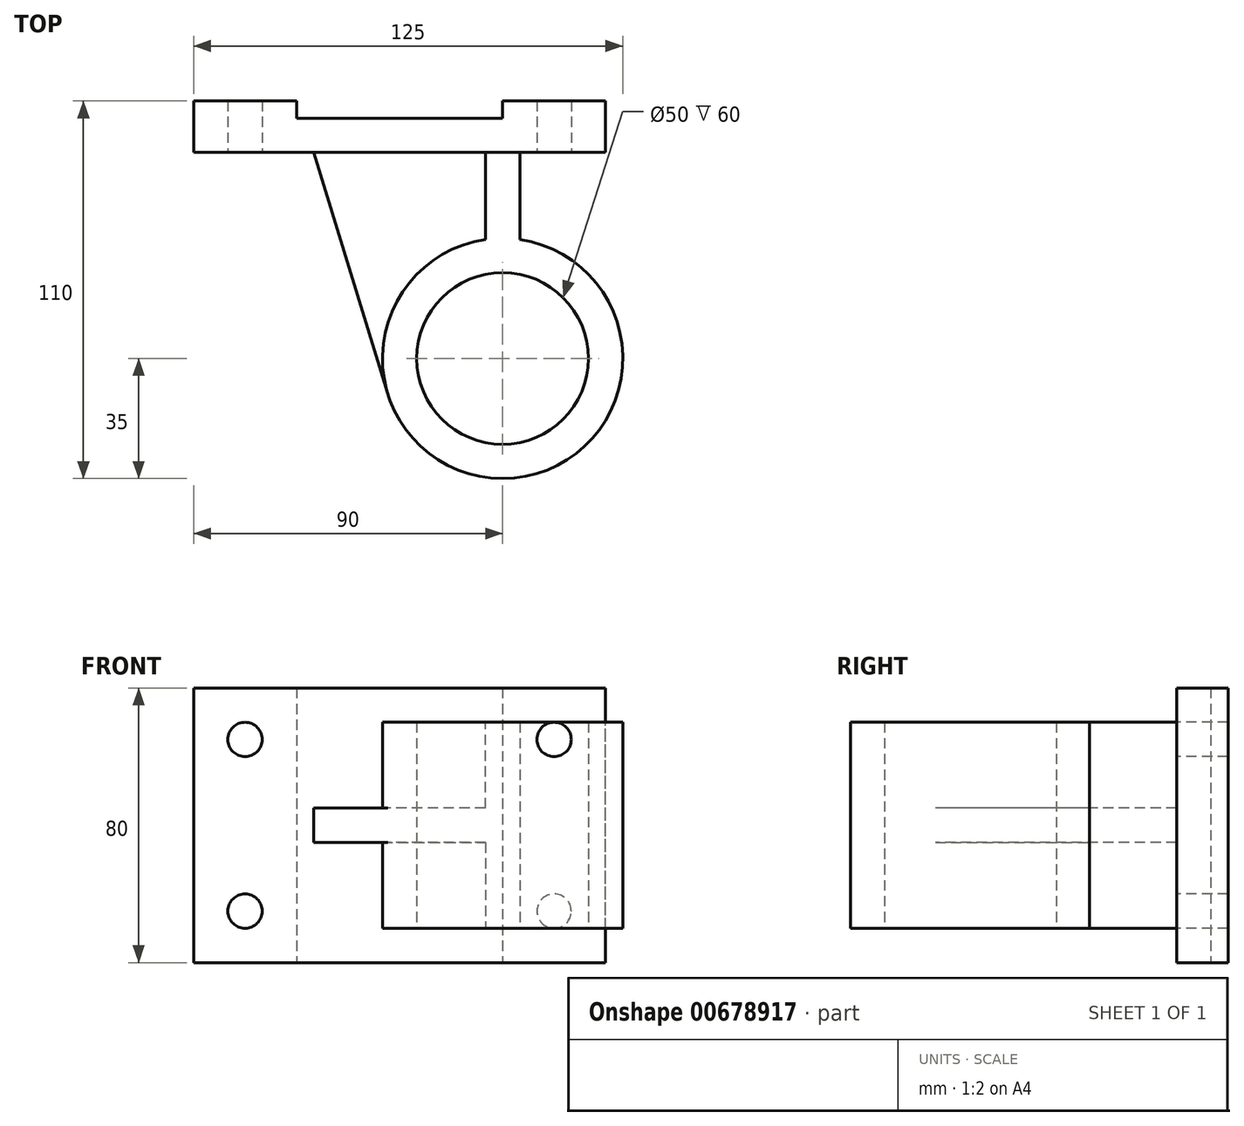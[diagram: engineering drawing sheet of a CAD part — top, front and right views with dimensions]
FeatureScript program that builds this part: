
annotation { "Feature Type Name" : "Feature", "Feature Type Description" : "" }
export const myFeature = defineFeature(function(context is Context, id is Id, definition is map)
    precondition{}
    {
        {
            var Q0;
            Q0=qCreatedBy(makeId("Front.planeOp"),FACE);
            var sketch = newSketch(context, id + "F0", { "sketchPlane" : qUnion([Q0])});
            skLineSegment(sketch, "E0.bottom", {"start": v(0, 0) * mm, "end": v(-120, 0) * mm});
            skLineSegment(sketch, "E0.top", {"start": v(0, 80) * mm, "end": v(-120, 80) * mm});
            skLineSegment(sketch, "E0.left", {"start": v(0, 0) * mm, "end": v(0, 80) * mm});
            skLineSegment(sketch, "E0.right", {"start": v(-120, 0) * mm, "end": v(-120, 80) * mm});
            skSolve(sketch);
        }
        {
            var Q0;
            Q0 = qSketchRegion(id + "F0", true);
            extrude(context, id + "F1", {"entities" : qUnion([Q0]), "depth" : 15 * mm, "offsetDistance" : 25 * mm});
        }
        {
            var Q0;
            Q0=makeQuery(id+"F1.opExtrude","CAP_FACE",FACE,{"disambiguationData":[OSD([sQuery(id+"F0.wireOp",EDGE,"E0.bottom"),sQuery(id+"F0.wireOp",EDGE,"E0.top"),sQuery(id+"F0.wireOp",EDGE,"E0.left"),sQuery(id+"F0.wireOp",EDGE,"E0.right")])],"isStart":false});
            var sketch = newSketch(context, id + "F2", { "sketchPlane" : qUnion([Q0])});
            skCircle(sketch, "E1", {"center": v(-105, 15) * mm, "radius": 5 * mm});
            skCircle(sketch, "E2", {"center": v(-105, 65) * mm, "radius": 5 * mm});
            skCircle(sketch, "E3", {"center": v(-15, 65) * mm, "radius": 5 * mm});
            skCircle(sketch, "E4", {"center": v(-15, 15) * mm, "radius": 5 * mm});
            skSolve(sketch);
        }
        {
            var Q0;
            Q0 = qSketchRegion(id + "F2", true);
            extrude(context, id + "F3", {"entities" : qUnion([Q0]), "operationType" : NewBodyOperationType.REMOVE, "endBound" : BoundingType.THROUGH_ALL, "oppositeDirection" : true, "depth" : 25 * mm, "offsetDistance" : 25 * mm});
        }
        {
            var Q0;
            Q0=makeQuery(id+"F1.opExtrude","SWEPT_FACE",FACE,{"disambiguationData":[OSD([sQuery(id+"F0.wireOp",EDGE,"E0.bottom")])]});
            var sketch = newSketch(context, id + "F4", { "sketchPlane" : qUnion([Q0])});
            skLineSegment(sketch, "E5", {"start": v(-60, 0) * mm, "end": v(-60, 5) * mm});
            skLineSegment(sketch, "E6", {"start": v(-60, 5) * mm, "end": v(-90, 5) * mm});
            skLineSegment(sketch, "E7", {"start": v(-90, 5) * mm, "end": v(-90, 0) * mm});
            skLineSegment(sketch, "E8", {"start": v(-90, 0) * mm, "end": v(-60, 0) * mm});
            skLineSegment(sketch, "E9.MirrorCS", {"start": v(-60, 5) * mm, "end": v(-30, 5) * mm});
            skLineSegment(sketch, "E10.MirrorCS", {"start": v(-30, 5) * mm, "end": v(-30, 0) * mm});
            skLineSegment(sketch, "E11.MirrorCS", {"start": v(-30, 0) * mm, "end": v(-60, 0) * mm});
            skSolve(sketch);
        }
        {
            var Q0;
            Q0 = qSketchRegion(id + "F4", true);
            extrude(context, id + "F5", {"entities" : qUnion([Q0]), "operationType" : NewBodyOperationType.REMOVE, "endBound" : BoundingType.THROUGH_ALL, "oppositeDirection" : true, "depth" : 25 * mm, "offsetDistance" : 25 * mm});
        }
        {
            var Q0;
            Q0=makeQuery(id+"F1.opExtrude","SWEPT_FACE",FACE,{"disambiguationData":[OSD([sQuery(id+"F0.wireOp",EDGE,"E0.bottom")])]});
            var sketch = newSketch(context, id + "F6", { "sketchPlane" : qUnion([Q0])});
            skLineSegment(sketch, "E12", {"start": v(-30, 15) * mm, "end": v(-30, 75) * mm});
            skCircle(sketch, "E13", {"center": v(-30, 75) * mm, "radius": 35 * mm});
            skLineSegment(sketch, "E14", {"start": v(-30, 15) * mm, "end": v(-35, 15) * mm});
            skLineSegment(sketch, "E15", {"start": v(-35, 15) * mm, "end": v(-35, 40.36) * mm});
            skLineSegment(sketch, "E16.MirrorCS", {"start": v(-30, 15) * mm, "end": v(-25, 15) * mm});
            skLineSegment(sketch, "E17.MirrorCS", {"start": v(-25, 15) * mm, "end": v(-25, 40.36) * mm});
            skCircle(sketch, "E18", {"center": v(-30, 75) * mm, "radius": 25 * mm});
            skLineSegment(sketch, "E19", {"start": v(-85, 15) * mm, "end": v(-63.46, 85.26) * mm});
            skLineSegment(sketch, "E20", {"start": v(-85, 15) * mm, "end": v(-35, 15) * mm});
            skSolve(sketch);
        }
        {
            var Q0;
            Q0 = qSketchRegion(id + "F6", true);
            extrude(context, id + "F7", {"entities" : qUnion([Q0]), "oppositeDirection" : true, "depth" : 70 * mm, "offsetDistance" : 25 * mm});
        }
        {
            var Q0;
            Q0=makeQuery(id+"F7.opExtrude","CAP_FACE",FACE,{"disambiguationData":[OSD([sQuery(id+"F6.wireOp",EDGE,"E13"),sQuery(id+"F6.wireOp",EDGE,"E14"),sQuery(id+"F6.wireOp",EDGE,"E16.MirrorCS"),sQuery(id+"F6.wireOp",EDGE,"E17.MirrorCS"),sQuery(id+"F6.wireOp",EDGE,"E18"),sQuery(id+"F6.wireOp",EDGE,"E19"),sQuery(id+"F6.wireOp",EDGE,"E20")])],"isStart":true});
            extrude(context, id + "F8", {"entities" : qUnion([Q0]), "operationType" : NewBodyOperationType.REMOVE, "oppositeDirection" : true, "depth" : 10 * mm, "offsetDistance" : 25 * mm});
        }
        {
            var Q0;
            {var subQ0=sQuery(id+"F6.wireOp",EDGE,"E15");Q0=makeQuery(id+"F6.imprint","IMPRINT",FACE,{"disambiguationData":[TD([[makeQuery(id+"F6.imprint","IMPRINT",EDGE,{"derivedFrom":subQ0}),1.0]])]});}
            extrude(context, id + "F9", {"entities" : qUnion([Q0]), "operationType" : NewBodyOperationType.REMOVE, "oppositeDirection" : true, "depth" : 35 * mm, "offsetDistance" : 25 * mm});
        }
        {
            var Q0;
            Q0=makeQuery(id+"F7.opExtrude","CAP_FACE",FACE,{"disambiguationData":[OSD([sQuery(id+"F6.wireOp",EDGE,"E13"),sQuery(id+"F6.wireOp",EDGE,"E14"),sQuery(id+"F6.wireOp",EDGE,"E16.MirrorCS"),sQuery(id+"F6.wireOp",EDGE,"E17.MirrorCS"),sQuery(id+"F6.wireOp",EDGE,"E18"),sQuery(id+"F6.wireOp",EDGE,"E19"),sQuery(id+"F6.wireOp",EDGE,"E20")])],"isStart":false});
            var sketch = newSketch(context, id + "F10", { "sketchPlane" : qUnion([Q0])});
            skLineSegment(sketch, "E21", {"start": v(-30, -75) * mm, "end": v(-30, -15) * mm});
            skCircle(sketch, "E22", {"center": v(-30, -75) * mm, "radius": 25 * mm});
            skCircle(sketch, "E23", {"center": v(-30, -75) * mm, "radius": 35 * mm});
            skLineSegment(sketch, "E24", {"start": v(-30, -15) * mm, "end": v(-25, -15) * mm});
            skLineSegment(sketch, "E25", {"start": v(-25, -15) * mm, "end": v(-25, -40.36) * mm});
            skLineSegment(sketch, "E26.MirrorCS", {"start": v(-30, -15) * mm, "end": v(-35, -15) * mm});
            skLineSegment(sketch, "E27.MirrorCS", {"start": v(-35, -15) * mm, "end": v(-35, -40.36) * mm});
            skLineSegment(sketch, "E28", {"start": v(-63.46, -85.26) * mm, "end": v(-85, -15) * mm});
            skLineSegment(sketch, "E29", {"start": v(-85, -15) * mm, "end": v(-35, -15) * mm});
            skSolve(sketch);
        }
        {
            var Q0;
            {var subQ2=sQuery(id+"F10.wireOp",EDGE,"E27.MirrorCS");Q0=makeQuery(id+"F10.imprint","IMPRINT",FACE,{"disambiguationData":[TD([[makeQuery(id+"F10.imprint","IMPRINT",EDGE,{"derivedFrom":subQ2}),-1.0]])]});}
            extrude(context, id + "F11", {"entities" : qUnion([Q0]), "operationType" : NewBodyOperationType.REMOVE, "oppositeDirection" : true, "depth" : 25 * mm, "offsetDistance" : 25 * mm});
        }
    });
